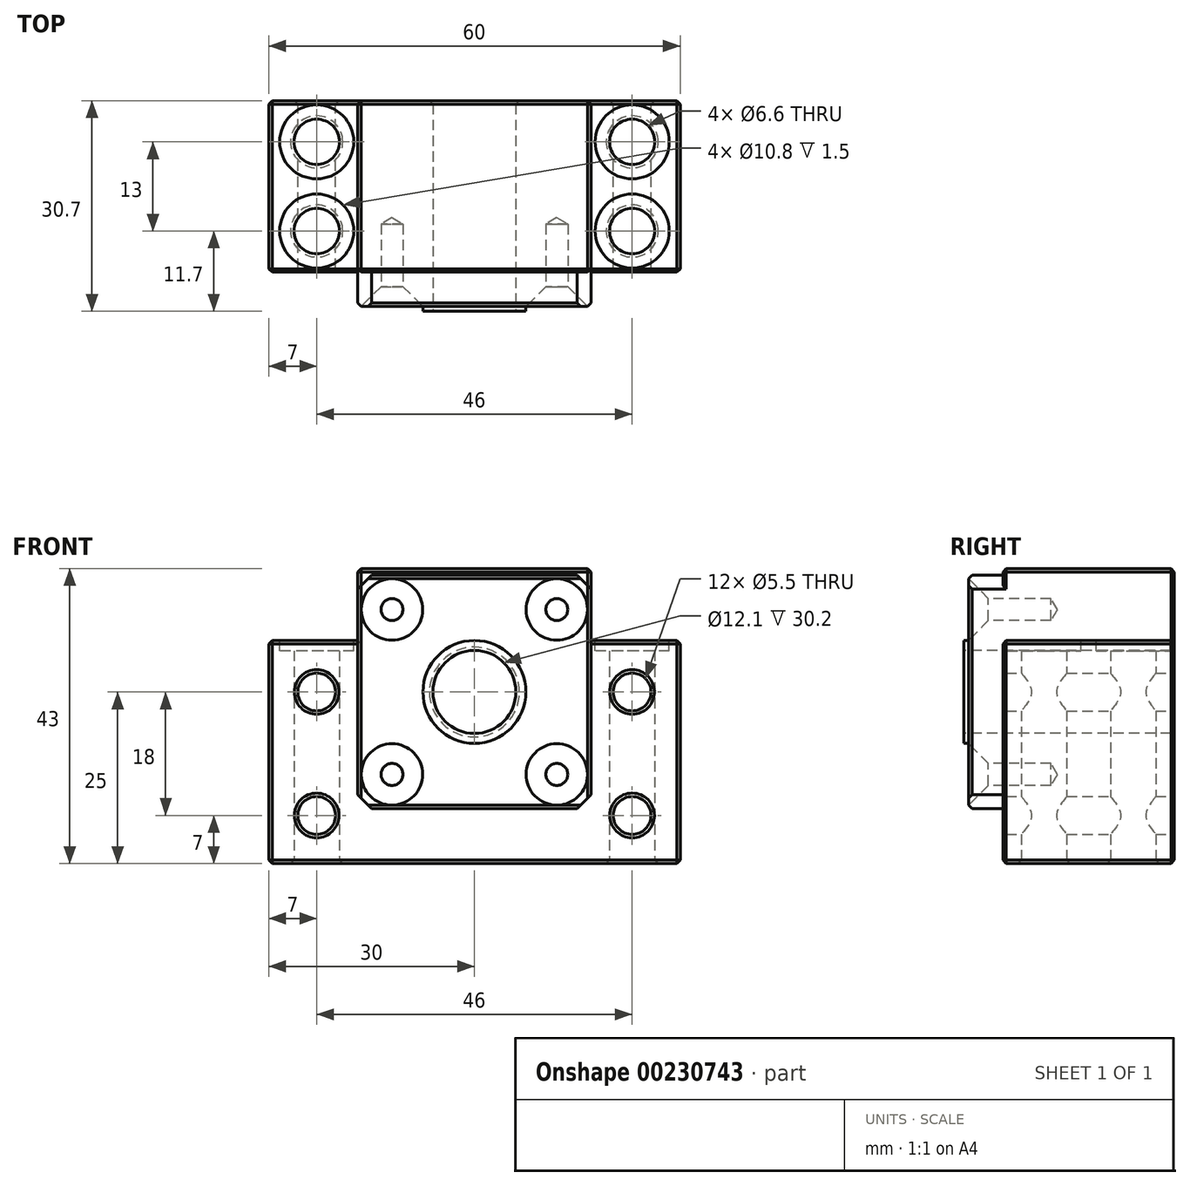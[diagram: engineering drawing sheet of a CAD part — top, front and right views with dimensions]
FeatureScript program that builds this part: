
annotation { "Feature Type Name" : "Feature", "Feature Type Description" : "" }
export const myFeature = defineFeature(function(context is Context, id is Id, definition is map)
    precondition{}
    {
        {
            var Q0;
            Q0=qCreatedBy(makeId("Front.planeOp"),FACE);
            var sketch = newSketch(context, id + "F0", { "sketchPlane" : qUnion([Q0])});
            skCircle(sketch, "E0", {"center": v(0, 0) * mm, "radius": 6.05 * mm});
            skCircle(sketch, "E1", {"center": v(0, 0) * mm, "radius": 7.5 * mm});
            skSolve(sketch);
        }
        {
            var Q0;
            Q0=qCreatedBy(makeId("Front.planeOp"),FACE);
            var sketch = newSketch(context, id + "F1", { "sketchPlane" : qUnion([Q0])});
            skLineSegment(sketch, "E2", {"start": v(-30, 7.5) * mm, "end": v(-30, -25) * mm});
            skLineSegment(sketch, "E3", {"start": v(-30, -25) * mm, "end": v(30, -25) * mm});
            skLineSegment(sketch, "E4", {"start": v(30, -25) * mm, "end": v(30, 7.5) * mm});
            skLineSegment(sketch, "E5", {"start": v(30, 7.5) * mm, "end": v(17, 7.5) * mm});
            skLineSegment(sketch, "E6", {"start": v(17, 7.5) * mm, "end": v(17, 18) * mm});
            skLineSegment(sketch, "E7", {"start": v(17, 18) * mm, "end": v(-17, 18) * mm});
            skLineSegment(sketch, "E8", {"start": v(-17, 18) * mm, "end": v(-17, 7.5) * mm});
            skLineSegment(sketch, "E9", {"start": v(-17, 7.5) * mm, "end": v(-30, 7.5) * mm});
            skLineSegment(sketch, "E10", {"start": v(0, 18) * mm, "end": v(0, -25) * mm, "construction": true});
            skCircle(sketch, "E11", {"center": v(-23, 0) * mm, "radius": 2.75 * mm});
            skCircle(sketch, "E12", {"center": v(-23, -18) * mm, "radius": 2.75 * mm});
            skCircle(sketch, "E13", {"center": v(23, -18) * mm, "radius": 2.75 * mm});
            skCircle(sketch, "E14", {"center": v(23, 0) * mm, "radius": 2.75 * mm});
            skSolve(sketch);
        }
        {
            var Q0;
            Q0 = qSketchRegion(id + "F1", true);
            extrude(context, id + "F2", {"entities" : qUnion([Q0]), "depth" : 25 * mm});
        }
        {
            var Q0;
            Q0=makeQuery(id+"F2.opExtrude","CAP_FACE",FACE,{"disambiguationData":[OSD([sQuery(id+"F1.wireOp",EDGE,"E2"),sQuery(id+"F1.wireOp",EDGE,"E3"),sQuery(id+"F1.wireOp",EDGE,"E4"),sQuery(id+"F1.wireOp",EDGE,"E5"),sQuery(id+"F1.wireOp",EDGE,"E6"),sQuery(id+"F1.wireOp",EDGE,"E7"),sQuery(id+"F1.wireOp",EDGE,"E8"),sQuery(id+"F1.wireOp",EDGE,"E9"),sQuery(id+"F1.wireOp",EDGE,"E11"),sQuery(id+"F1.wireOp",EDGE,"E12"),sQuery(id+"F1.wireOp",EDGE,"E13"),sQuery(id+"F1.wireOp",EDGE,"E14")])],"isStart":false});
            var sketch = newSketch(context, id + "F3", { "sketchPlane" : qUnion([Q0])});
            skLineSegment(sketch, "E15.bottom", {"start": v(17, 17) * mm, "end": v(-17, 17) * mm});
            skLineSegment(sketch, "E15.top", {"start": v(17, -17) * mm, "end": v(-17, -17) * mm});
            skLineSegment(sketch, "E15.left", {"start": v(17, 17) * mm, "end": v(17, -17) * mm});
            skLineSegment(sketch, "E15.right", {"start": v(-17, 17) * mm, "end": v(-17, -17) * mm});
            skPoint(sketch, "E15.middle", {"position": v(0, 0) * mm});
            skSolve(sketch);
        }
        {
            var Q0;
            Q0 = qSketchRegion(id + "F3", true);
            extrude(context, id + "F4", {"entities" : qUnion([Q0]), "operationType" : NewBodyOperationType.ADD, "depth" : 5 * mm});
        }
        {
            var Q0;
            Q0=makeQuery(id+"F4.opExtrude","CAP_FACE",FACE,{"disambiguationData":[OSD([sQuery(id+"F3.wireOp",EDGE,"E15.bottom"),sQuery(id+"F3.wireOp",EDGE,"E15.top"),sQuery(id+"F3.wireOp",EDGE,"E15.left"),sQuery(id+"F3.wireOp",EDGE,"E15.right")])],"isStart":false});
            var sketch = newSketch(context, id + "F5", { "sketchPlane" : qUnion([Q0])});
            skCircle(sketch, "E16", {"center": v(0, 0) * mm, "radius": 17 * mm, "construction": true});
            skLineSegment(sketch, "E17", {"start": v(-17, 17) * mm, "end": v(17, -17) * mm, "construction": true});
            skLineSegment(sketch, "E18", {"start": v(17, 17) * mm, "end": v(-17, -17) * mm, "construction": true});
            skPoint(sketch, "E19", {"position": v(-12.02, 12.02) * mm});
            skPoint(sketch, "E20", {"position": v(12.02, 12.02) * mm});
            skPoint(sketch, "E21", {"position": v(12.02, -12.02) * mm});
            skPoint(sketch, "E22", {"position": v(-12.02, -12.02) * mm});
            skSolve(sketch);
        }
        {
            var Q0;
            Q0=sQuery(id+"F5.wireOp",VERTEX,"E19");
            var Q1;
            Q1=sQuery(id+"F5.wireOp",VERTEX,"E20");
            var Q2;
            Q2=sQuery(id+"F5.wireOp",VERTEX,"E21");
            var Q3;
            Q3=sQuery(id+"F5.wireOp",VERTEX,"E22");
            var Q4;
            Q4=makeQuery(id+"F2.opExtrude","SWEPT_BODY",BODY,{"disambiguationData":[OSD([sQuery(id+"F1.wireOp",EDGE,"E2"),sQuery(id+"F1.wireOp",EDGE,"E3"),sQuery(id+"F1.wireOp",EDGE,"E4"),sQuery(id+"F1.wireOp",EDGE,"E5"),sQuery(id+"F1.wireOp",EDGE,"E6"),sQuery(id+"F1.wireOp",EDGE,"E7"),sQuery(id+"F1.wireOp",EDGE,"E8"),sQuery(id+"F1.wireOp",EDGE,"E9"),sQuery(id+"F1.wireOp",EDGE,"E11"),sQuery(id+"F1.wireOp",EDGE,"E12"),sQuery(id+"F1.wireOp",EDGE,"E13"),sQuery(id+"F1.wireOp",EDGE,"E14")])]});
            hole(context, id + "F6", {"style" : HoleStyle.C_SINK, "endStyle" : HoleEndStyle.BLIND, "standardTappedOrClearance" : lookupTablePath({ "standard" : "ISO", "engagement" : "75%", "pitch" : "0.75 mm", "size" : "M4", "type" : "Tapped" }), "standardBlindInLast" : lookupTablePath({ "standard" : "ISO", "engagement" : "75%", "pitch" : "0.75 mm", "size" : "M4", "type" : "Tapped" }), "holeDiameter" : 3.2 * mm, "cSinkDiameter" : 8.96 * mm, "cSinkAngle" : 90 * degree, "holeDepth" : 12 * mm, "locations" : qUnion([Q0, Q1, Q2, Q3]), "scope" : qUnion([Q4])});
        }
        {
            var Q0;
            Q0=makeQuery(id+"F4.opExtrude","CAP_FACE",FACE,{"disambiguationData":[OSD([sQuery(id+"F3.wireOp",EDGE,"E15.bottom"),sQuery(id+"F3.wireOp",EDGE,"E15.top"),sQuery(id+"F3.wireOp",EDGE,"E15.left"),sQuery(id+"F3.wireOp",EDGE,"E15.right")])],"isStart":false});
            var sketch = newSketch(context, id + "F7", { "sketchPlane" : qUnion([Q0])});
            skCircle(sketch, "E23", {"center": v(0, 0) * mm, "radius": 6.05 * mm});
            skSolve(sketch);
        }
        {
            var Q0;
            Q0 = qSketchRegion(id + "F7", true);
            extrude(context, id + "F8", {"entities" : qUnion([Q0]), "operationType" : NewBodyOperationType.REMOVE, "endBound" : BoundingType.UP_TO_NEXT, "oppositeDirection" : true, "depth" : 25 * mm});
        }
        {
            var Q0;
            Q0 = qSketchRegion(id + "F0", true);
            extrude(context, id + "F9", {"entities" : qUnion([Q0]), "operationType" : NewBodyOperationType.ADD, "depth" : 30.7 * mm});
        }
        {
            var Q0;
            Q0=makeQuery(id+"F2.opExtrude","SWEPT_FACE",FACE,{"disambiguationData":[OSD([sQuery(id+"F1.wireOp",EDGE,"E3")])]});
            var sketch = newSketch(context, id + "F10", { "sketchPlane" : qUnion([Q0])});
            skLineSegment(sketch, "E24", {"start": v(0, 25) * mm, "end": v(0, 0) * mm, "construction": true});
            skLineSegment(sketch, "E25", {"start": v(-30, 12.5) * mm, "end": v(30, 12.5) * mm, "construction": true});
            skCircle(sketch, "E26", {"center": v(-23, 19) * mm, "radius": 3.3 * mm});
            skCircle(sketch, "E27", {"center": v(-23, 6) * mm, "radius": 3.3 * mm});
            skCircle(sketch, "E28", {"center": v(23, 6) * mm, "radius": 3.3 * mm});
            skCircle(sketch, "E29", {"center": v(23, 19) * mm, "radius": 3.3 * mm});
            skSolve(sketch);
        }
        {
            var Q0;
            Q0 = qSketchRegion(id + "F10", true);
            var Q1;
            Q1=makeQuery(id+"F2.opExtrude","SWEPT_FACE",FACE,{"disambiguationData":[OSD([sQuery(id+"F1.wireOp",EDGE,"E9")])]});
            extrude(context, id + "F11", {"entities" : qUnion([Q0]), "operationType" : NewBodyOperationType.REMOVE, "endBound" : BoundingType.UP_TO_SURFACE, "oppositeDirection" : true, "endBoundEntityFace" : qUnion([Q1]), "depth" : 25 * mm});
        }
        {
            var Q0;
            Q0=makeQuery(id+"F2.opExtrude","CAP_FACE",FACE,{"disambiguationData":[OSD([sQuery(id+"F1.wireOp",EDGE,"E2"),sQuery(id+"F1.wireOp",EDGE,"E3"),sQuery(id+"F1.wireOp",EDGE,"E4"),sQuery(id+"F1.wireOp",EDGE,"E5"),sQuery(id+"F1.wireOp",EDGE,"E6"),sQuery(id+"F1.wireOp",EDGE,"E7"),sQuery(id+"F1.wireOp",EDGE,"E8"),sQuery(id+"F1.wireOp",EDGE,"E9"),sQuery(id+"F1.wireOp",EDGE,"E11"),sQuery(id+"F1.wireOp",EDGE,"E12"),sQuery(id+"F1.wireOp",EDGE,"E13"),sQuery(id+"F1.wireOp",EDGE,"E14")])],"isStart":true});
            var Q1;
            Q1=makeQuery(id+"F2.opExtrude","SWEPT_FACE",FACE,{"disambiguationData":[OSD([sQuery(id+"F1.wireOp",EDGE,"E7")])]});
            var Q2;
            Q2=makeQuery(id+"F2.opExtrude","SWEPT_FACE",FACE,{"disambiguationData":[OSD([sQuery(id+"F1.wireOp",EDGE,"E4")])]});
            var Q3;
            Q3=makeQuery(id+"F2.opExtrude","SWEPT_FACE",FACE,{"disambiguationData":[OSD([sQuery(id+"F1.wireOp",EDGE,"E2")])]});
            var Q4;
            Q4=makeQuery(id+"F2.opExtrude","SWEPT_FACE",FACE,{"disambiguationData":[OSD([sQuery(id+"F1.wireOp",EDGE,"E3")])]});
            var Q5;
            Q5=makeQuery(id+"F2.opExtrude","CAP_EDGE",EDGE,{"disambiguationData":[OSD([sQuery(id+"F1.wireOp",EDGE,"E5")])],"isStart":false});
            var Q6;
            Q6=makeQuery(id+"F2.opExtrude","CAP_EDGE",EDGE,{"disambiguationData":[OSD([sQuery(id+"F1.wireOp",EDGE,"E9")])],"isStart":false});
            var Q7;
            Q7=makeQuery(id+"F2.opExtrude","CAP_EDGE",EDGE,{"disambiguationData":[OSD([sQuery(id+"F1.wireOp",EDGE,"E6")])],"isStart":false});
            var Q8;
            Q8=makeQuery(id+"F2.opExtrude","CAP_EDGE",EDGE,{"disambiguationData":[OSD([sQuery(id+"F1.wireOp",EDGE,"E8")])],"isStart":false});
            var Q9;
            Q9=makeQuery(id+"F2.opExtrude","CAP_EDGE",EDGE,{"disambiguationData":[OSD([sQuery(id+"F1.wireOp",EDGE,"E11")])],"isStart":false});
            var Q10;
            Q10=makeQuery(id+"F2.opExtrude","CAP_EDGE",EDGE,{"disambiguationData":[OSD([sQuery(id+"F1.wireOp",EDGE,"E12")])],"isStart":false});
            var Q11;
            Q11=makeQuery(id+"F2.opExtrude","CAP_EDGE",EDGE,{"disambiguationData":[OSD([sQuery(id+"F1.wireOp",EDGE,"E13")])],"isStart":false});
            var Q12;
            Q12=makeQuery(id+"F2.opExtrude","CAP_EDGE",EDGE,{"disambiguationData":[OSD([sQuery(id+"F1.wireOp",EDGE,"E14")])],"isStart":false});
            var Q13;
            Q13=makeQuery(id+"F4.opExtrude","CAP_EDGE",EDGE,{"disambiguationData":[OSD([sQuery(id+"F3.wireOp",EDGE,"E15.right")])],"isStart":false});
            var Q14;
            Q14=makeQuery(id+"F4.opExtrude","CAP_EDGE",EDGE,{"disambiguationData":[OSD([sQuery(id+"F3.wireOp",EDGE,"E15.left")])],"isStart":false});
            var Q15;
            Q15=makeQuery(id+"F4.opExtrude","CAP_EDGE",EDGE,{"disambiguationData":[OSD([sQuery(id+"F3.wireOp",EDGE,"E15.top")])],"isStart":false});
            var Q16;
            Q16=makeQuery(id+"F4.opExtrude","CAP_EDGE",EDGE,{"disambiguationData":[OSD([sQuery(id+"F3.wireOp",EDGE,"E15.bottom")])],"isStart":false});
            chamfer(context, id + "F12", {"entities" : qUnion([Q0, Q1, Q2, Q3, Q4, Q5, Q6, Q7, Q8, Q9, Q10, Q11, Q12, Q13, Q14, Q15, Q16]), "width" : 0.5 * mm, "tangentPropagation" : true});
        }
        {
            var Q0;
            Q0=makeQuery(id+"F4.opExtrude","SWEPT_EDGE",EDGE,{"disambiguationData":[OSD([sQuery(id+"F3.wireOp",EDGE,"E15.bottom"),sQuery(id+"F3.wireOp",EDGE,"E15.right")])]});
            var Q1;
            Q1=makeQuery(id+"F4.opExtrude","SWEPT_EDGE",EDGE,{"disambiguationData":[OSD([sQuery(id+"F3.wireOp",EDGE,"E15.bottom"),sQuery(id+"F3.wireOp",EDGE,"E15.left")])]});
            var Q2;
            Q2=makeQuery(id+"F4.opExtrude","SWEPT_EDGE",EDGE,{"disambiguationData":[OSD([sQuery(id+"F3.wireOp",EDGE,"E15.top"),sQuery(id+"F3.wireOp",EDGE,"E15.left")])]});
            var Q3;
            Q3=makeQuery(id+"F4.opExtrude","SWEPT_EDGE",EDGE,{"disambiguationData":[OSD([sQuery(id+"F3.wireOp",EDGE,"E15.top"),sQuery(id+"F3.wireOp",EDGE,"E15.right")])]});
            chamfer(context, id + "F13", {"entities" : qUnion([Q0, Q1, Q2, Q3]), "width" : 2 * mm, "tangentPropagation" : true});
        }
        {
            var Q0;
            Q0=makeQuery(id+"F2.opExtrude","SWEPT_FACE",FACE,{"disambiguationData":[OSD([sQuery(id+"F1.wireOp",EDGE,"E9")])]});
            var sketch = newSketch(context, id + "F14", { "sketchPlane" : qUnion([Q0])});
            skCircle(sketch, "E30", {"center": v(-23, -6) * mm, "radius": 5.4 * mm});
            skCircle(sketch, "E31", {"center": v(-23, -19) * mm, "radius": 5.4 * mm});
            skCircle(sketch, "E32", {"center": v(23, -19) * mm, "radius": 5.4 * mm});
            skCircle(sketch, "E33", {"center": v(23, -6) * mm, "radius": 5.4 * mm});
            skSolve(sketch);
        }
        {
            var Q0;
            Q0 = qSketchRegion(id + "F14", true);
            extrude(context, id + "F15", {"entities" : qUnion([Q0]), "operationType" : NewBodyOperationType.REMOVE, "oppositeDirection" : true, "depth" : 1.5 * mm});
        }
    });
